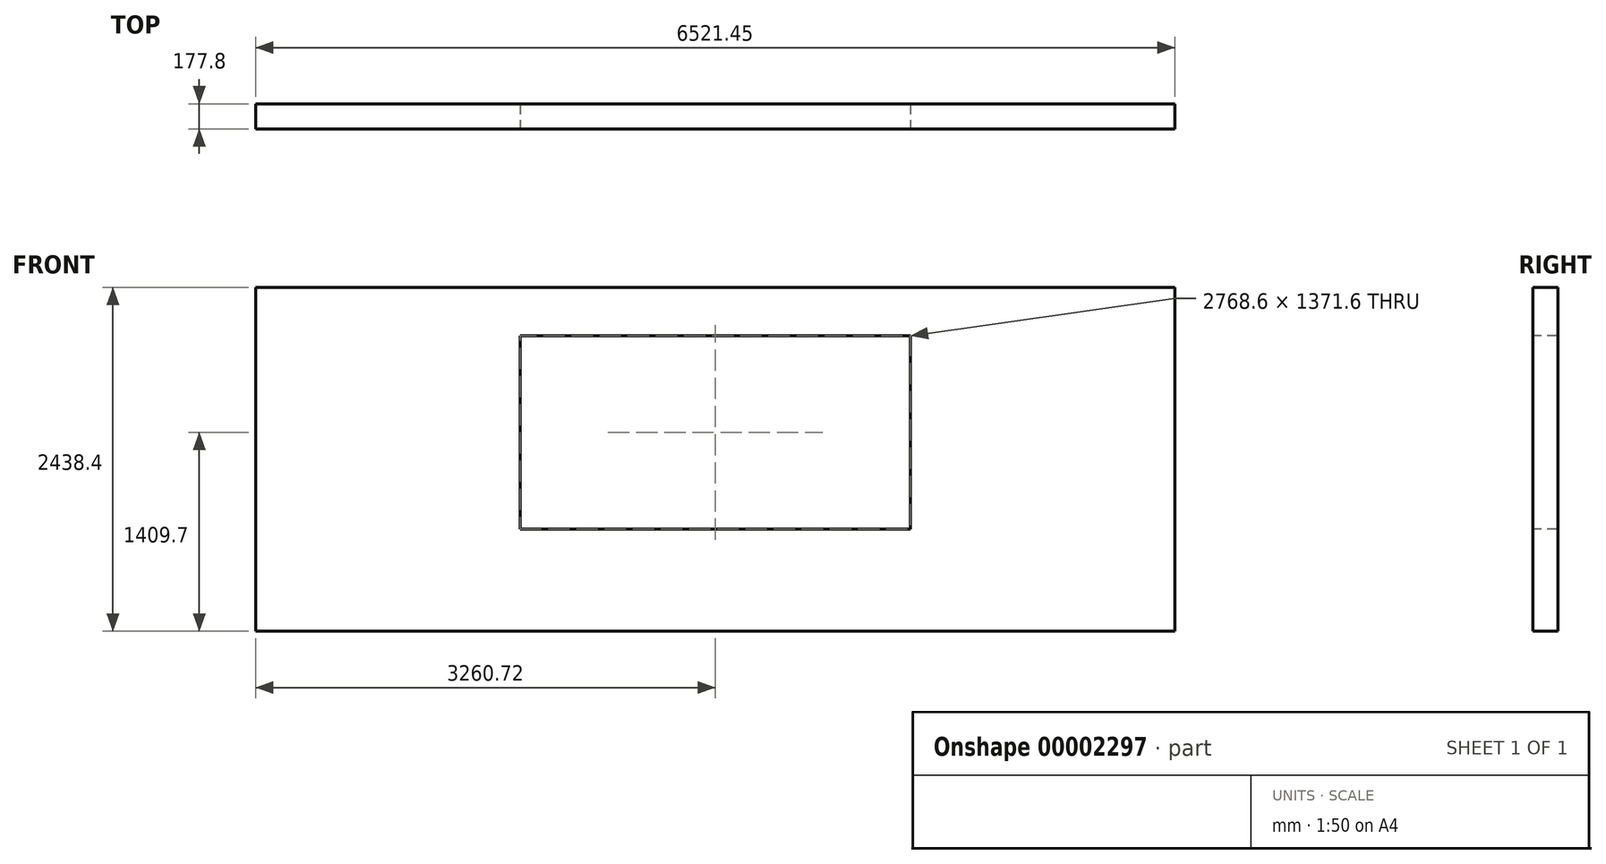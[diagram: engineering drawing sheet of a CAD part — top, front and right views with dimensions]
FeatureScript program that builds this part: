
annotation { "Feature Type Name" : "Feature", "Feature Type Description" : "" }
export const myFeature = defineFeature(function(context is Context, id is Id, definition is map)
    precondition{}
    {
        {
            var Q0;
            Q0=qCreatedBy(makeId("Front.planeOp"),FACE);
            var sketch = newSketch(context, id + "F0", { "sketchPlane" : qUnion([Q0])});
            skLineSegment(sketch, "E0.bottom", {"start": v(0, 0) * mm, "end": v(6521.45, 0) * mm});
            skLineSegment(sketch, "E0.top", {"start": v(0, 2438.4) * mm, "end": v(6521.45, 2438.4) * mm});
            skLineSegment(sketch, "E0.left", {"start": v(0, 0) * mm, "end": v(0, 2438.4) * mm});
            skLineSegment(sketch, "E0.right", {"start": v(6521.45, 0) * mm, "end": v(6521.45, 2438.4) * mm});
            skSolve(sketch);
        }
        {
            var Q0;
            Q0=qSketchRegion(id+"F0",true);
            extrude(context, id + "F1", {"entities" : qUnion([Q0]), "depth" : 177.8 * mm});
        }
        {
            var Q0;
            Q0=makeQuery(id+"F1.opExtrude","CAP_FACE",FACE,{"disambiguationData":[OSD([sQuery(id+"F0.wireOp",EDGE,"E0.bottom"),sQuery(id+"F0.wireOp",EDGE,"E0.top"),sQuery(id+"F0.wireOp",EDGE,"E0.left"),sQuery(id+"F0.wireOp",EDGE,"E0.right")])],"isStart":false});
            var sketch = newSketch(context, id + "F2", { "sketchPlane" : qUnion([Q0])});
            skLineSegment(sketch, "E1.bottom", {"start": v(1876.43, 723.9) * mm, "end": v(4645.03, 723.9) * mm});
            skLineSegment(sketch, "E1.top", {"start": v(1876.43, 2095.5) * mm, "end": v(4645.03, 2095.5) * mm});
            skLineSegment(sketch, "E1.left", {"start": v(1876.43, 723.9) * mm, "end": v(1876.43, 2095.5) * mm});
            skLineSegment(sketch, "E1.right", {"start": v(4645.03, 723.9) * mm, "end": v(4645.03, 2095.5) * mm});
            skSolve(sketch);
        }
        {
            var Q0;
            Q0=makeQuery(id+"F2.imprint","IMPRINT",FACE,{"disambiguationData":[TD([[makeQuery(id+"F2.imprint","IMPRINT",EDGE,{"derivedFrom":sQuery(id+"F2.wireOp",EDGE,"E1.bottom")}),1.0]])]});
            extrude(context, id + "F3", {"entities" : qUnion([Q0]), "operationType" : NewBodyOperationType.REMOVE, "oppositeDirection" : true, "depth" : 177.8 * mm});
        }
    });
